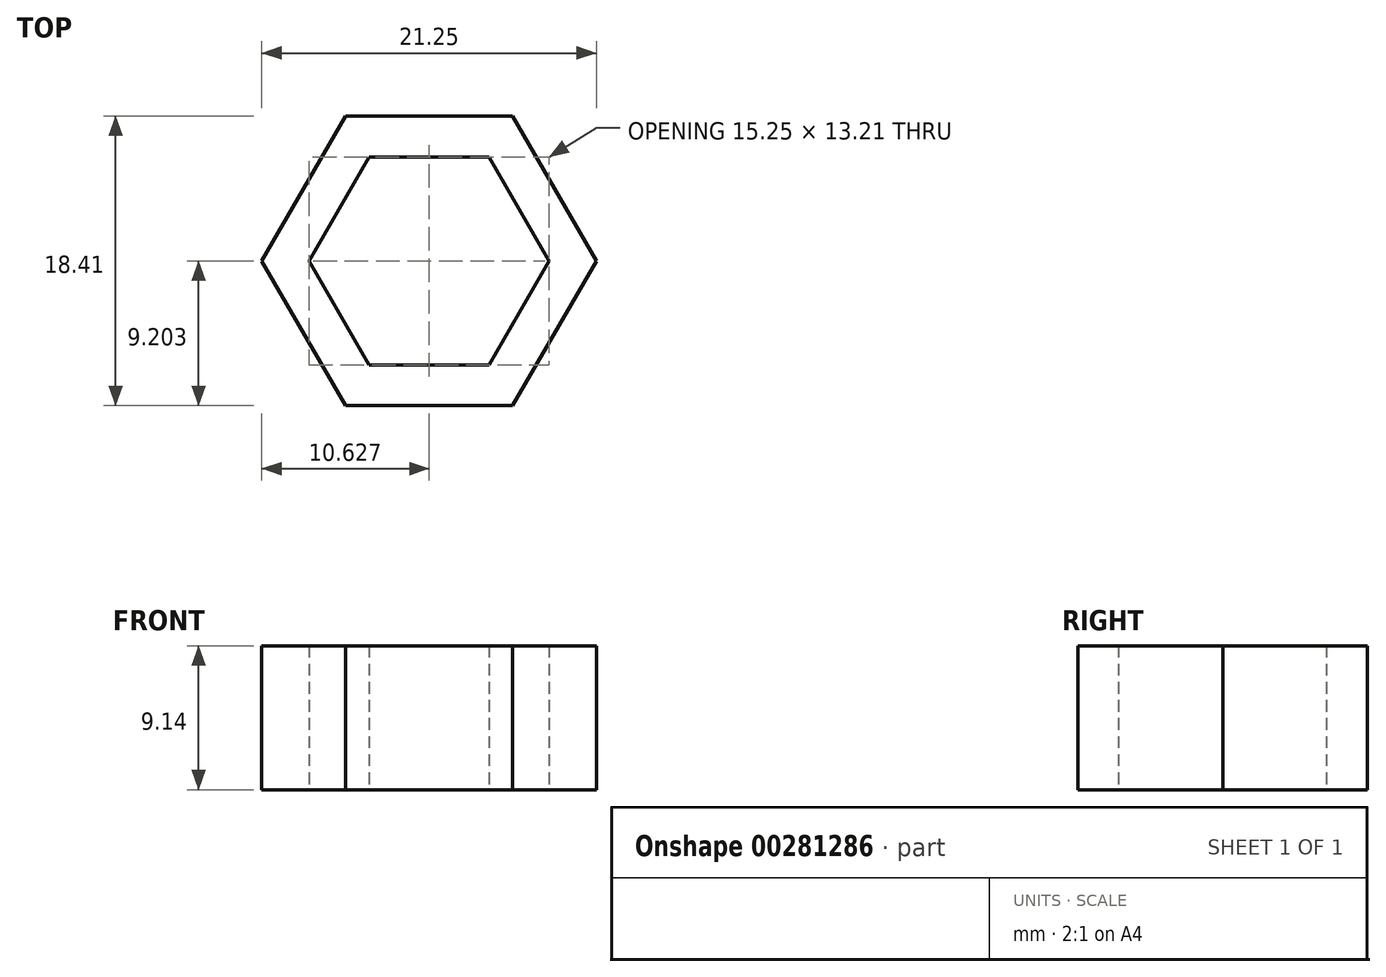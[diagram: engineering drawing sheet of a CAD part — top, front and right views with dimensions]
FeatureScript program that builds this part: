
annotation { "Feature Type Name" : "Feature", "Feature Type Description" : "" }
export const myFeature = defineFeature(function(context is Context, id is Id, definition is map)
    precondition{}
    {
        {
            var Q0;
            Q0=qCreatedBy(makeId("Top.planeOp"),FACE);
            var sketch = newSketch(context, id + "F0", { "sketchPlane" : qUnion([Q0])});
            skCircle(sketch, "E0.cCircle", {"center": v(-0.15, 15.2) * mm, "radius": 6.6 * mm, "construction": true});
            skLineSegment(sketch, "E0.0", {"start": v(-3.97, 21.8) * mm, "end": v(3.66, 21.8) * mm});
            skLineSegment(sketch, "E0.1", {"start": v(3.66, 21.8) * mm, "end": v(7.47, 15.2) * mm});
            skLineSegment(sketch, "E0.2", {"start": v(7.47, 15.2) * mm, "end": v(3.66, 8.6) * mm});
            skLineSegment(sketch, "E0.3", {"start": v(3.66, 8.6) * mm, "end": v(-3.97, 8.6) * mm});
            skLineSegment(sketch, "E0.4", {"start": v(-3.97, 8.6) * mm, "end": v(-7.78, 15.2) * mm});
            skLineSegment(sketch, "E0.5", {"start": v(-7.78, 15.2) * mm, "end": v(-3.97, 21.8) * mm});
            skPoint(sketch, "E0.0.midPoint", {"position": v(-0.15, 21.8) * mm});
            skCircle(sketch, "E1.cCircle", {"center": v(-0.15, 15.2) * mm, "radius": 9.2 * mm, "construction": true});
            skLineSegment(sketch, "E1.0", {"start": v(-5.47, 24.4) * mm, "end": v(5.16, 24.4) * mm});
            skLineSegment(sketch, "E1.1", {"start": v(5.16, 24.4) * mm, "end": v(10.47, 15.2) * mm});
            skLineSegment(sketch, "E1.2", {"start": v(10.47, 15.2) * mm, "end": v(5.16, 6) * mm});
            skLineSegment(sketch, "E1.3", {"start": v(5.16, 6) * mm, "end": v(-5.47, 6) * mm});
            skLineSegment(sketch, "E1.4", {"start": v(-5.47, 6) * mm, "end": v(-10.78, 15.2) * mm});
            skLineSegment(sketch, "E1.5", {"start": v(-10.78, 15.2) * mm, "end": v(-5.47, 24.4) * mm});
            skSolve(sketch);
        }
        {
            var Q0;
            Q0=makeQuery(id+"F0.imprint","IMPRINT",FACE,{"disambiguationData":[TD([[makeQuery(id+"F0.imprint","IMPRINT",EDGE,{"derivedFrom":sQuery(id+"F0.wireOp",EDGE,"E0.0")}),1.0]])]});
            extrude(context, id + "F1", {"entities" : qUnion([Q0]), "depth" : 9.14 * mm});
        }
    });
